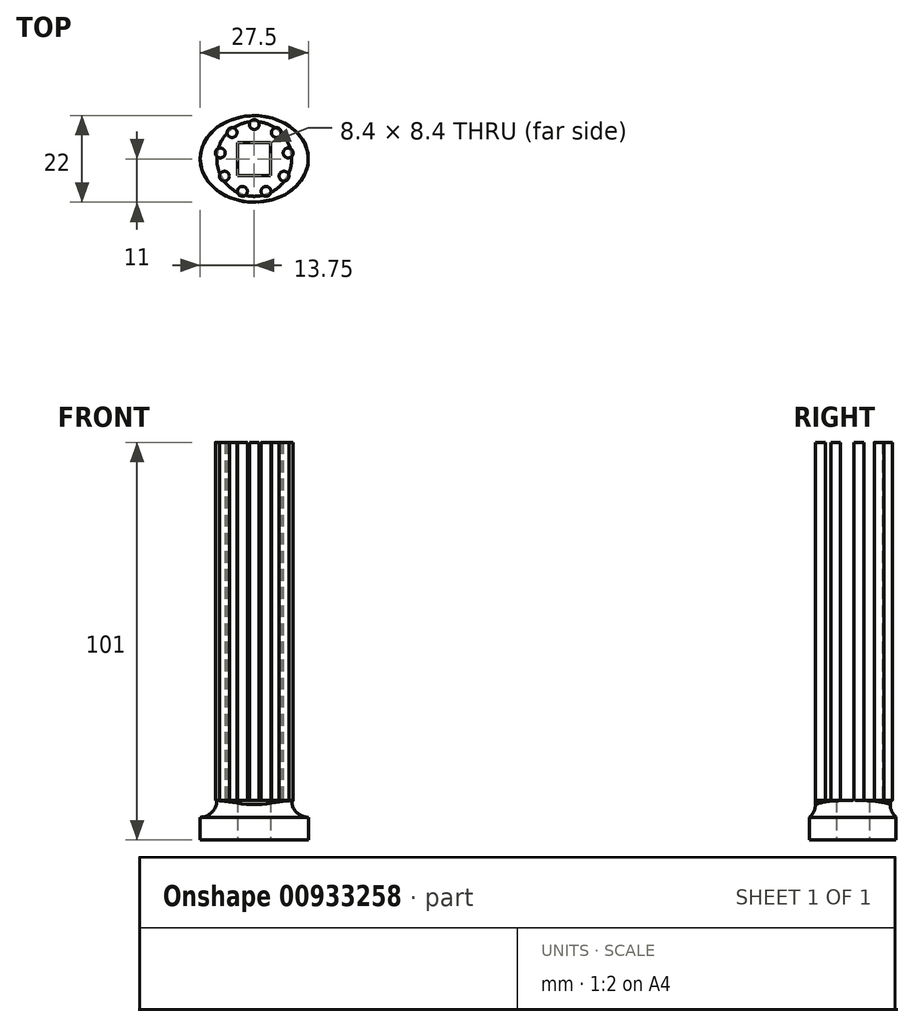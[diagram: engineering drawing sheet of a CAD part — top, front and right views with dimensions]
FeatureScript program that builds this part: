
annotation { "Feature Type Name" : "Feature", "Feature Type Description" : "" }
export const myFeature = defineFeature(function(context is Context, id is Id, definition is map)
    precondition{}
    {
        {
            var Q0;
            Q0=qCreatedBy(makeId("Top.planeOp"),FACE);
            var sketch = newSketch(context, id + "F0", { "sketchPlane" : qUnion([Q0])});
            skCircle(sketch, "E0", {"center": v(0, 0) * mm, "radius": 11 * mm});
            skCircle(sketch, "E1", {"center": v(0, 0) * mm, "radius": 3.9 * mm, "construction": true});
            skLineSegment(sketch, "E2.bottom", {"start": v(-3.89, 3.9) * mm, "end": v(3.9, 3.9) * mm});
            skLineSegment(sketch, "E2.top", {"start": v(-3.9, -3.9) * mm, "end": v(3.89, -3.9) * mm});
            skLineSegment(sketch, "E2.left", {"start": v(-3.89, 3.9) * mm, "end": v(-3.9, -3.9) * mm});
            skLineSegment(sketch, "E2.right", {"start": v(3.9, 3.9) * mm, "end": v(3.89, -3.9) * mm});
            skSolve(sketch);
        }
        {
            var Q0;
            Q0 = qSketchRegion(id + "F0", true);
            extrude(context, id + "F1", {"entities" : qUnion([Q0]), "depth" : 10 * mm, "offsetDistance" : 25 * mm});
        }
        {
            var Q0;
            Q0=makeQuery(id+"F1.opExtrude","CAP_FACE",FACE,{"disambiguationData":[OSD([sQuery(id+"F0.wireOp",EDGE,"E0"),sQuery(id+"F0.wireOp",EDGE,"E1")])],"isStart":false});
            var sketch = newSketch(context, id + "F2", { "sketchPlane" : qUnion([Q0])});
            skCircle(sketch, "E3", {"center": v(0, 8.75) * mm, "radius": 1.25 * mm});
            skCircle(sketch, "E4.1.0", {"center": v(-5.62, 6.7) * mm, "radius": 1.25 * mm});
            skCircle(sketch, "E4.2.0", {"center": v(-8.62, 1.52) * mm, "radius": 1.25 * mm});
            skCircle(sketch, "E4.3.0", {"center": v(-7.58, -4.37) * mm, "radius": 1.25 * mm});
            skCircle(sketch, "E4.4.0", {"center": v(-3, -8.22) * mm, "radius": 1.25 * mm});
            skCircle(sketch, "E4.5.0", {"center": v(3, -8.22) * mm, "radius": 1.25 * mm});
            skCircle(sketch, "E4.6.0", {"center": v(7.58, -4.38) * mm, "radius": 1.25 * mm});
            skCircle(sketch, "E4.7.0", {"center": v(8.62, 1.52) * mm, "radius": 1.25 * mm});
            skCircle(sketch, "E4.8.0", {"center": v(5.62, 6.7) * mm, "radius": 1.25 * mm});
            skPoint(sketch, "E4.center", {"position": v(0, 0) * mm});
            skSolve(sketch);
        }
        {
            var Q0;
            Q0 = qSketchRegion(id + "F2", true);
            extrude(context, id + "F3", {"entities" : qUnion([Q0]), "operationType" : NewBodyOperationType.ADD, "depth" : 91 * mm, "offsetDistance" : 25 * mm});
        }
        {
            var Q0;
            Q0=qCreatedBy(makeId("Top.planeOp"),FACE);
            var sketch = newSketch(context, id + "F4", { "sketchPlane" : qUnion([Q0])});
            skCircle(sketch, "E5", {"center": v(0, 0) * mm, "radius": 11 * mm});
            skLineSegment(sketch, "E6.bottom", {"start": v(4.2, -4.2) * mm, "end": v(-4.2, -4.2) * mm});
            skLineSegment(sketch, "E6.top", {"start": v(4.2, 4.2) * mm, "end": v(-4.2, 4.2) * mm});
            skLineSegment(sketch, "E6.left", {"start": v(4.2, -4.2) * mm, "end": v(4.2, 4.2) * mm});
            skLineSegment(sketch, "E6.right", {"start": v(-4.2, -4.2) * mm, "end": v(-4.2, 4.2) * mm});
            skSolve(sketch);
        }
        {
            var Q0;
            Q0 = qSketchRegion(id + "F4", true);
            extrude(context, id + "F5", {"entities" : qUnion([Q0]), "depth" : 10 * mm, "offsetDistance" : 25 * mm});
        }
        {
            var Q0;
            Q0=makeQuery(id+"F5.opExtrude","CAP_FACE",FACE,{"disambiguationData":[OSD([sQuery(id+"F4.wireOp",EDGE,"E5"),sQuery(id+"F4.wireOp",EDGE,"E6.bottom"),sQuery(id+"F4.wireOp",EDGE,"E6.top"),sQuery(id+"F4.wireOp",EDGE,"E6.left"),sQuery(id+"F4.wireOp",EDGE,"E6.right")])],"isStart":false});
            var sketch = newSketch(context, id + "F6", { "sketchPlane" : qUnion([Q0])});
            skCircle(sketch, "E7", {"center": v(0, 0) * mm, "radius": 20.14 * mm});
            skCircle(sketch, "E8", {"center": v(0, 0) * mm, "radius": 9.5 * mm});
            skSolve(sketch);
        }
        {
            var Q0;
            Q0 = qSketchRegion(id + "F6", true);
            extrude(context, id + "F7", {"entities" : qUnion([Q0]), "operationType" : NewBodyOperationType.REMOVE, "oppositeDirection" : true, "depth" : 1.5 * mm, "offsetDistance" : 25 * mm});
        }
        {
            var Q0;
            Q0=makeQuery(id+"F7.boolean.opBoolean","COPY",EDGE,{"derivedFrom":makeQuery(id+"F7.opExtrude","CAP_EDGE",EDGE,{"disambiguationData":[OSD([sQuery(id+"F6.wireOp",EDGE,"E8")])],"isStart":false})});
            fillet(context, id + "F8", {"entities" : qUnion([Q0]), "radius" : 1.5 * mm, "tangentPropagation" : true, "allowEdgeOverflow" : false});
        }
        {
            var Q0;
            Q0=makeQuery(id+"F5.opExtrude","SWEPT_FACE",FACE,{"disambiguationData":[OSD([sQuery(id+"F4.wireOp",EDGE,"E6.right")])]});
            extrude(context, id + "F9", {"entities" : qUnion([Q0]), "operationType" : NewBodyOperationType.ADD, "depth" : 9.4 * mm, "offsetDistance" : 25 * mm});
        }
        {
            var Q0;
            {var subQ0=sQuery(id+"F4.wireOp",EDGE,"E6.right");Q0=makeQuery(id+"F9.boolean.opBoolean","MERGE",FACE,{"derivedFrom":[makeQuery(id+"F5.opExtrude","CAP_FACE",FACE,{"disambiguationData":[OSD([sQuery(id+"F4.wireOp",EDGE,"E5"),sQuery(id+"F4.wireOp",EDGE,"E6.bottom"),sQuery(id+"F4.wireOp",EDGE,"E6.top"),sQuery(id+"F4.wireOp",EDGE,"E6.left"),subQ0])],"isStart":true}),makeQuery(id+"F9.opExtrude","SWEPT_FACE",FACE,{"disambiguationData":[OSD([subQ0]),TDD([makeQuery(id+"F5.opExtrude","CAP_EDGE",EDGE,{"disambiguationData":[OSD([subQ0])],"isStart":true})])]})]});}
            var sketch = newSketch(context, id + "F10", { "sketchPlane" : qUnion([Q0])});
            skCircle(sketch, "E9", {"center": v(0, 0) * mm, "radius": 3.65 * mm});
            skSolve(sketch);
        }
        {
            var Q0;
            Q0 = qSketchRegion(id + "F10", true);
            extrude(context, id + "F11", {"entities" : qUnion([Q0]), "operationType" : NewBodyOperationType.REMOVE, "oppositeDirection" : true, "depth" : 25 * mm, "offsetDistance" : 25 * mm});
        }
        {
            var Q0;
            Q0=qCreatedBy(makeId("Top.planeOp"),FACE);
            var sketch = newSketch(context, id + "F12", { "sketchPlane" : qUnion([Q0])});
            skEllipse(sketch, "E10", {"center": v(0, 0) * mm, "majorRadius": 11 * mm, "minorRadius": 13.75 * mm, "majorAxis": v(0, 1)});
            skLineSegment(sketch, "E11.bottom", {"start": v(4.2, 4.2) * mm, "end": v(-4.2, 4.2) * mm});
            skLineSegment(sketch, "E11.top", {"start": v(4.2, -4.2) * mm, "end": v(-4.2, -4.2) * mm});
            skLineSegment(sketch, "E11.left", {"start": v(4.2, 4.2) * mm, "end": v(4.2, -4.2) * mm});
            skLineSegment(sketch, "E11.right", {"start": v(-4.2, 4.2) * mm, "end": v(-4.2, -4.2) * mm});
            skSolve(sketch);
        }
        {
            var Q0;
            Q0 = qSketchRegion(id + "F12", true);
            extrude(context, id + "F13", {"entities" : qUnion([Q0]), "operationType" : NewBodyOperationType.ADD, "depth" : (10 - 4.25) * mm, "offsetDistance" : 25 * mm});
        }
        {
            var Q0;
            {var subQ0=sQuery(id+"F4.wireOp",EDGE,"E6.right");Q0=makeQuery(id+"F9.boolean.opBoolean","MERGE",FACE,{"derivedFrom":[makeQuery(id+"F5.opExtrude","CAP_FACE",FACE,{"disambiguationData":[OSD([sQuery(id+"F4.wireOp",EDGE,"E5"),sQuery(id+"F4.wireOp",EDGE,"E6.bottom"),sQuery(id+"F4.wireOp",EDGE,"E6.top"),sQuery(id+"F4.wireOp",EDGE,"E6.left"),subQ0])],"isStart":false}),makeQuery(id+"F9.opExtrude","SWEPT_FACE",FACE,{"disambiguationData":[OSD([subQ0]),TDD([makeQuery(id+"F5.opExtrude","CAP_EDGE",EDGE,{"disambiguationData":[OSD([subQ0])],"isStart":false})])]})]});}
            var sketch = newSketch(context, id + "F14", { "sketchPlane" : qUnion([Q0])});
            skCircle(sketch, "E12.0", {"center": v(0, 0) * mm, "radius": 9.5 * mm});
            skCircle(sketch, "E13", {"center": v(0, 0) * mm, "radius": 14.24 * mm});
            skSolve(sketch);
        }
        {
            var Q0;
            Q0 = qSketchRegion(id + "F14", true);
            extrude(context, id + "F15", {"entities" : qUnion([Q0]), "operationType" : NewBodyOperationType.REMOVE, "oppositeDirection" : true, "depth" : 4.25 * mm, "offsetDistance" : 25 * mm});
        }
        {
            var Q0;
            Q0=makeQuery(id+"F15.boolean.opBoolean","COPY",EDGE,{"derivedFrom":makeQuery(id+"F15.opExtrude","CAP_EDGE",EDGE,{"disambiguationData":[OSD([sQuery(id+"F14.wireOp",EDGE,"E12.0")])],"isStart":false})});
            fillet(context, id + "F16", {"entities" : qUnion([Q0]), "radius" : 4.25 * mm, "tangentPropagation" : true, "allowEdgeOverflow" : false});
        }
        {
            var Q0;
            {var subQ0=sQuery(id+"F4.wireOp",EDGE,"E6.right");Q0=makeQuery(id+"F13.boolean.opBoolean","MERGE",FACE,{"derivedFrom":[makeQuery(id+"F9.boolean.opBoolean","MERGE",FACE,{"derivedFrom":[makeQuery(id+"F5.opExtrude","CAP_FACE",FACE,{"disambiguationData":[OSD([sQuery(id+"F4.wireOp",EDGE,"E5"),sQuery(id+"F4.wireOp",EDGE,"E6.bottom"),sQuery(id+"F4.wireOp",EDGE,"E6.top"),sQuery(id+"F4.wireOp",EDGE,"E6.left"),subQ0])],"isStart":true}),makeQuery(id+"F9.opExtrude","SWEPT_FACE",FACE,{"disambiguationData":[OSD([subQ0]),TDD([makeQuery(id+"F5.opExtrude","CAP_EDGE",EDGE,{"disambiguationData":[OSD([subQ0])],"isStart":true})])]})]}),makeQuery(id+"F13.opExtrude","CAP_FACE",FACE,{"disambiguationData":[OSD([sQuery(id+"F12.wireOp",EDGE,"E10"),sQuery(id+"F12.wireOp",EDGE,"E11.bottom"),sQuery(id+"F12.wireOp",EDGE,"E11.top"),sQuery(id+"F12.wireOp",EDGE,"E11.left"),sQuery(id+"F12.wireOp",EDGE,"E11.right")])],"isStart":true})]});}
            var sketch = newSketch(context, id + "F17", { "sketchPlane" : qUnion([Q0])});
            skLineSegment(sketch, "E14.bottom", {"start": v(-4.2, -4.2) * mm, "end": v(4.2, -4.2) * mm});
            skLineSegment(sketch, "E14.top", {"start": v(-4.2, 4.2) * mm, "end": v(4.2, 4.2) * mm});
            skLineSegment(sketch, "E14.left", {"start": v(-4.2, -4.2) * mm, "end": v(-4.2, 4.2) * mm});
            skLineSegment(sketch, "E14.right", {"start": v(4.2, -4.2) * mm, "end": v(4.2, 4.2) * mm});
            skPoint(sketch, "E14.middle", {"position": v(0, 0) * mm});
            skSolve(sketch);
        }
        {
            var Q0;
            Q0 = qSketchRegion(id + "F17", true);
            extrude(context, id + "F18", {"entities" : qUnion([Q0]), "operationType" : NewBodyOperationType.REMOVE, "oppositeDirection" : true, "depth" : 25 * mm, "offsetDistance" : 25 * mm});
        }
    });
